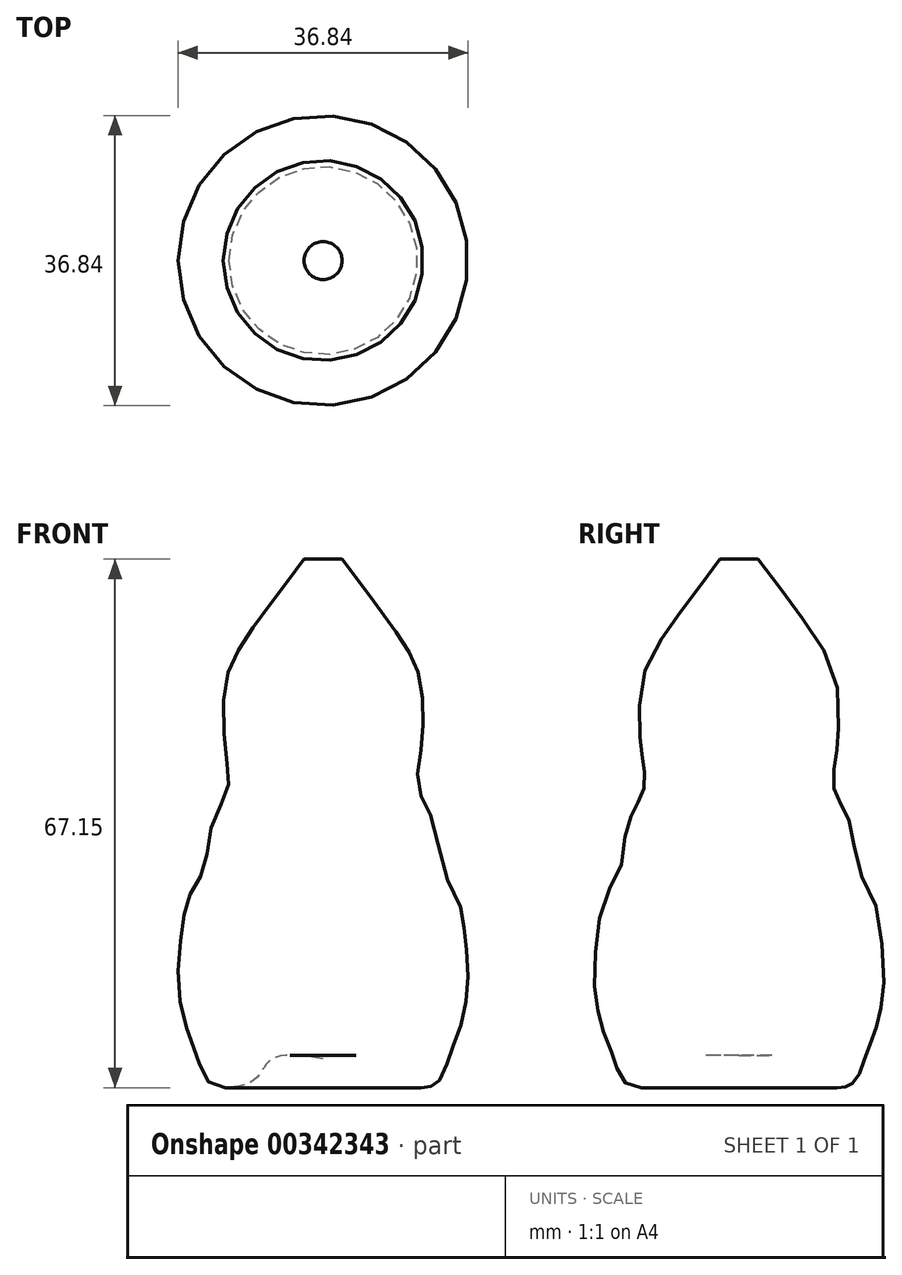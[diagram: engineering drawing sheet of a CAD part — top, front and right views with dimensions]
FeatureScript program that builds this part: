
annotation { "Feature Type Name" : "Feature", "Feature Type Description" : "" }
export const myFeature = defineFeature(function(context is Context, id is Id, definition is map)
    precondition{}
    {
        {
            var Q0;
            Q0=qCreatedBy(makeId("Front.planeOp"),FACE);
            var sketch = newSketch(context, id + "F0", { "sketchPlane" : qUnion([Q0])});
            skLineSegment(sketch, "E0", {"start": v(0, 75.37) * mm, "end": v(0, -61.67) * mm, "construction": true});
            skSolve(sketch);
        }
        {
            var Q0;
            Q0=qCreatedBy(makeId("Front.planeOp"),FACE);
            var sketch = newSketch(context, id + "F1", { "sketchPlane" : qUnion([Q0])});
            skFitSpline(sketch, "E1", {"points": [v(0, 0) * mm, v(-6.45, 0) * mm, v(-8.46, -2.42) * mm, v(-11.69, -3.63) * mm, v(-14.51, -3.02) * mm, v(-15.92, 0) * mm, v(-16.93, 2.62) * mm, v(-18.34, 8.67) * mm, v(-17.94, 16.32) * mm, v(-16.93, 20.76) * mm, v(-15.12, 24.18) * mm, v(-14.1, 29.83) * mm, v(-12.1, 34.26) * mm, v(-12.3, 38.3) * mm, v(-12.5, 47.16) * mm, v(-10.48, 52.4) * mm, v(-6.65, 57.84) * mm, v(-2.42, 63.48) * mm], "startDerivative": vector(-114.63, 17.73) * mm, "endDerivative": vector(60.31, 80.3) * mm});
            skLineSegment(sketch, "E2", {"start": v(-2.42, 63.48) * mm, "end": v(0, 63.48) * mm});
            skLineSegment(sketch, "E3", {"start": v(0, 63.48) * mm, "end": v(0, 0) * mm});
            skSolve(sketch);
        }
        {
            var Q0;
            Q0=makeQuery(id+"F1.imprint","IMPRINT",FACE,{"disambiguationData":[TD([[makeQuery(id+"F1.imprint","IMPRINT",EDGE,{"derivedFrom":sQuery(id+"F1.wireOp",EDGE,"E1")}),-1.0]])]});
            var Q1;
            Q1=sQuery(id+"F0.wireOp",EDGE,"E0");
            revolve(context, id + "F2", {"entities" : qUnion([Q0]), "axis" : qUnion([Q1]), "revolveType" : RevolveType.FULL});
        }
    });
